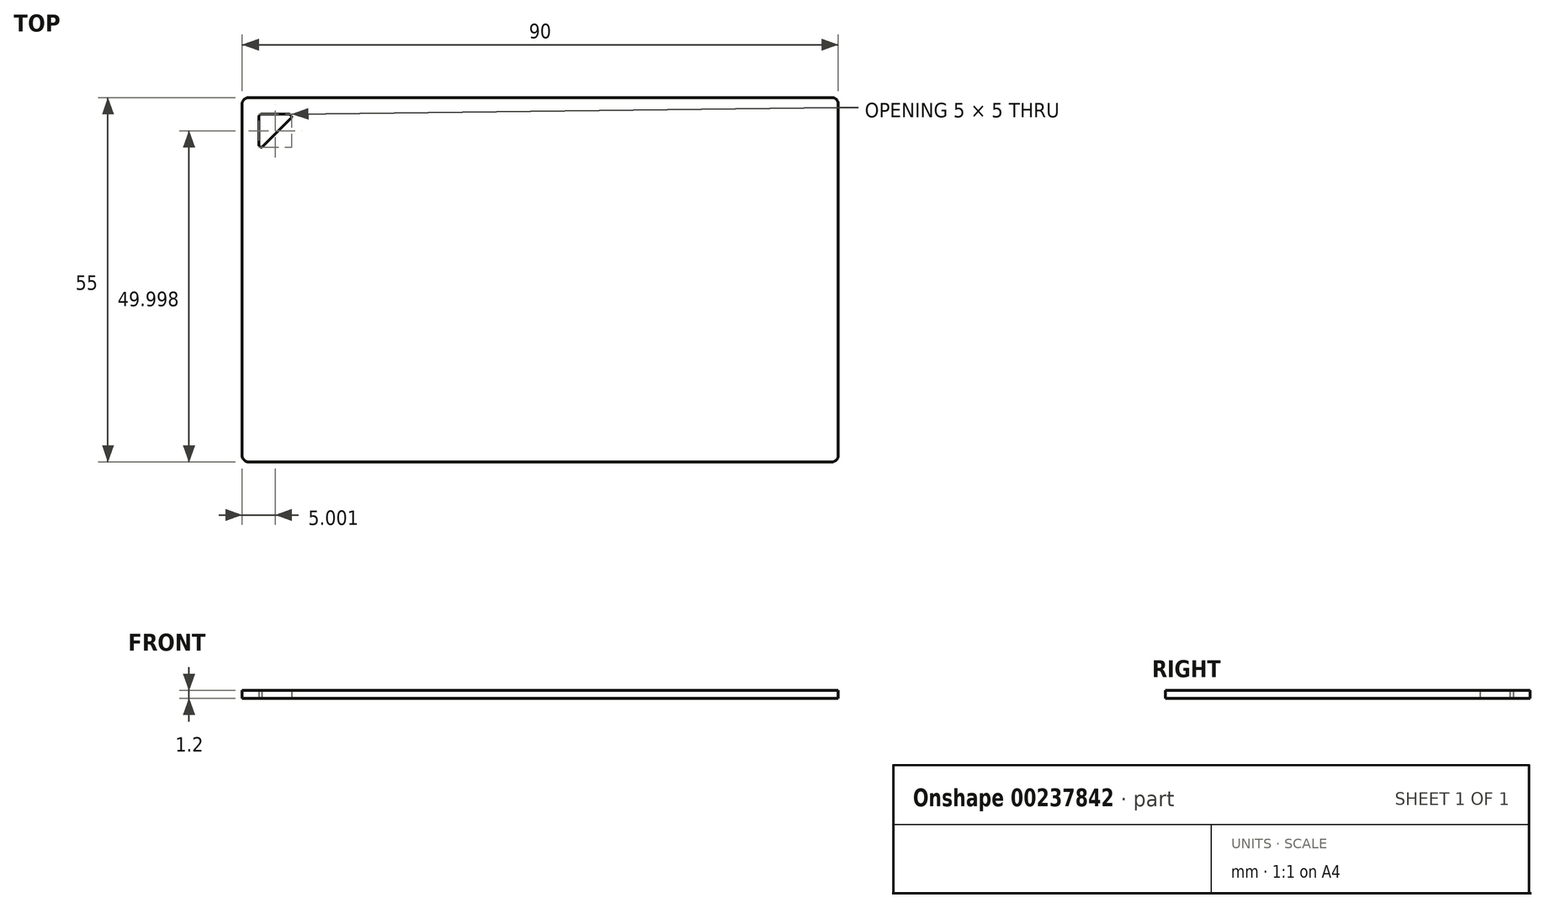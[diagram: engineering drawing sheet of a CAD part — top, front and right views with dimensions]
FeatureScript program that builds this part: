
annotation { "Feature Type Name" : "Feature", "Feature Type Description" : "" }
export const myFeature = defineFeature(function(context is Context, id is Id, definition is map)
    precondition{}
    {
        {
            var Q0;
            Q0=qCreatedBy(makeId("Top.planeOp"),FACE);
            var sketch = newSketch(context, id + "F0", { "sketchPlane" : qUnion([Q0])});
            skLineSegment(sketch, "E0.bottom", {"start": v(1, 0) * mm, "end": v(89, 0) * mm});
            skLineSegment(sketch, "E0.top", {"start": v(1, 55) * mm, "end": v(89, 55) * mm});
            skLineSegment(sketch, "E0.left", {"start": v(0, 1) * mm, "end": v(0, 54) * mm});
            skLineSegment(sketch, "E0.right", {"start": v(90, 1) * mm, "end": v(90, 54) * mm});
            skPoint(sketch, "E1.visualSharp", {"position": v(0, 55) * mm});
            skArc(sketch, "E1.filletArc", {"start": v(1, 55) * mm, "mid": v(0.3, 54.7) * mm, "end": v(0, 54) * mm});
            skPoint(sketch, "E2.visualSharp", {"position": v(90, 55) * mm});
            skArc(sketch, "E2.filletArc", {"start": v(90, 54) * mm, "mid": v(89.7, 54.7) * mm, "end": v(89, 55) * mm});
            skPoint(sketch, "E3.visualSharp", {"position": v(90, 0) * mm});
            skArc(sketch, "E3.filletArc", {"start": v(89, 0) * mm, "mid": v(89.7, 0.3) * mm, "end": v(90, 1) * mm});
            skPoint(sketch, "E4.visualSharp", {"position": v(0, 0) * mm});
            skArc(sketch, "E4.filletArc", {"start": v(0, 1) * mm, "mid": v(0.3, 0.3) * mm, "end": v(1, 0) * mm});
            skLineSegment(sketch, "E5", {"start": v(4.6, 55) * mm, "end": v(4.6, 52.5) * mm, "construction": true});
            skLineSegment(sketch, "E6", {"start": v(0, 52.4) * mm, "end": v(2.5, 52.4) * mm, "construction": true});
            skLineSegment(sketch, "E7.bottom", {"start": v(3, 52.5) * mm, "end": v(7, 52.5) * mm});
            skLineSegment(sketch, "E7.left", {"start": v(2.5, 52) * mm, "end": v(2.5, 48) * mm});
            skPoint(sketch, "E8.visualSharp", {"position": v(2.5, 52.5) * mm});
            skArc(sketch, "E8.filletArc", {"start": v(3, 52.5) * mm, "mid": v(2.65, 52.35) * mm, "end": v(2.5, 52) * mm});
            skPoint(sketch, "E9.visualSharp", {"position": v(7.5, 52.5) * mm});
            skArc(sketch, "E9.filletArc", {"start": v(7.5, 52) * mm, "mid": v(7.35, 52.35) * mm, "end": v(7, 52.5) * mm});
            skPoint(sketch, "E10.visualSharp", {"position": v(2.5, 47.5) * mm});
            skArc(sketch, "E10.filletArc", {"start": v(2.5, 48) * mm, "mid": v(2.65, 47.64) * mm, "end": v(3, 47.5) * mm});
            skLineSegment(sketch, "E11", {"start": v(3, 47.5) * mm, "end": v(7.5, 52) * mm});
            skSolve(sketch);
        }
        {
            var Q0;
            Q0=makeQuery(id+"F0.imprint","IMPRINT",FACE,{"disambiguationData":[TD([[makeQuery(id+"F0.imprint","IMPRINT",EDGE,{"derivedFrom":sQuery(id+"F0.wireOp",EDGE,"E0.bottom")}),1.0]])]});
            extrude(context, id + "F1", {"entities" : qUnion([Q0]), "depth" : 1.2 * mm});
        }
    });
